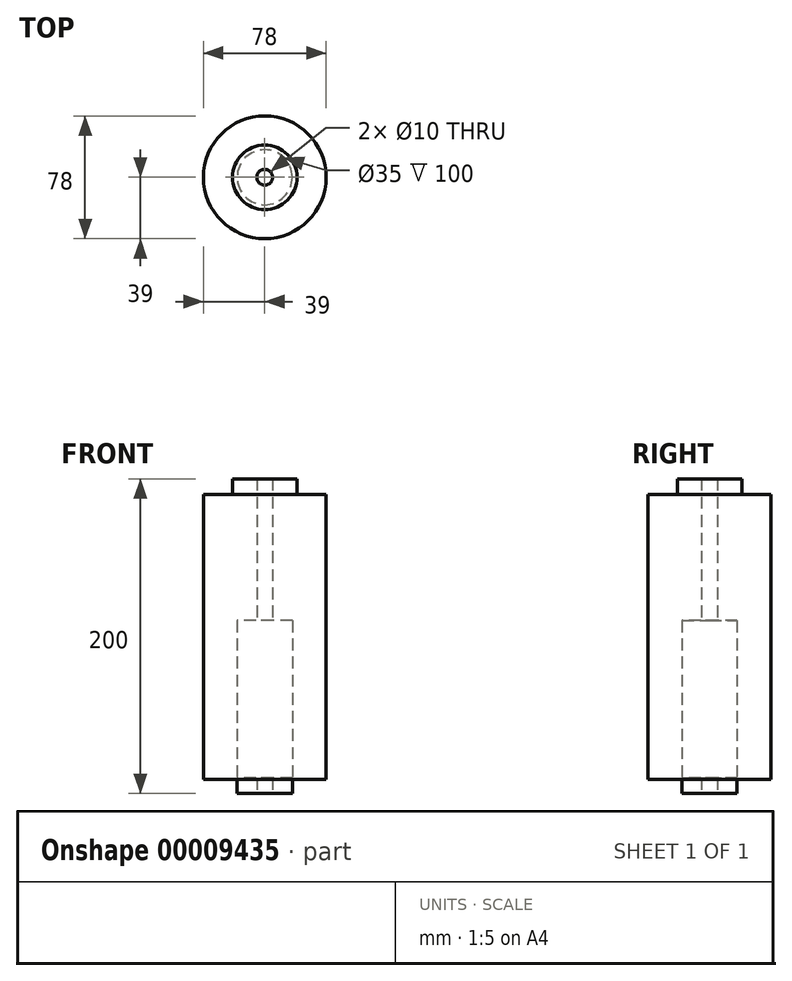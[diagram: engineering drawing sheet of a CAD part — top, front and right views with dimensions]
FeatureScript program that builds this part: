
annotation { "Feature Type Name" : "Feature", "Feature Type Description" : "" }
export const myFeature = defineFeature(function(context is Context, id is Id, definition is map)
    precondition{}
    {
        {
            var Q0;
            Q0=qCreatedBy(makeId("Top.planeOp"),FACE);
            var sketch = newSketch(context, id + "F0", { "sketchPlane" : qUnion([Q0])});
            skCircle(sketch, "E0", {"center": v(0, 0) * mm, "radius": 5 * mm});
            skCircle(sketch, "E1", {"center": v(0, 0) * mm, "radius": 17.5 * mm});
            skCircle(sketch, "E2", {"center": v(0, 0) * mm, "radius": 20.5 * mm});
            skCircle(sketch, "E3", {"center": v(0, 0) * mm, "radius": 39 * mm});
            skSolve(sketch);
        }
        {
            var Q0;
            Q0=makeQuery(id+"F0.imprint","IMPRINT",FACE,{"disambiguationData":[TD([[makeQuery(id+"F0.imprint","IMPRINT",EDGE,{"derivedFrom":sQuery(id+"F0.wireOp",EDGE,"E0")}),-1.0]])]});
            extrude(context, id + "F1", {"entities" : qUnion([Q0]), "depth" : 10 * mm});
        }
        {
            var Q0;
            Q0=makeQuery(id+"F0.imprint","IMPRINT",FACE,{"disambiguationData":[TD([[makeQuery(id+"F0.imprint","IMPRINT",EDGE,{"derivedFrom":sQuery(id+"F0.wireOp",EDGE,"E2")}),-1.0]])]});
            var Q1;
            Q1=makeQuery(id+"F0.imprint","IMPRINT",FACE,{"disambiguationData":[TD([[makeQuery(id+"F0.imprint","IMPRINT",EDGE,{"derivedFrom":sQuery(id+"F0.wireOp",EDGE,"E1")}),-1.0]])]});
            extrude(context, id + "F2", {"entities" : qUnion([Q0, Q1]), "operationType" : NewBodyOperationType.ADD, "depth" : 110 * mm, "hasSecondDirection" : true, "secondDirectionOppositeDirection" : false, "secondDirectionDepth" : 9 * mm});
        }
        {
            var Q0;
            Q0=makeQuery(id+"F2.opExtrude","CAP_FACE",FACE,{"disambiguationData":[OSD([sQuery(id+"F0.wireOp",EDGE,"E1"),sQuery(id+"F0.wireOp",EDGE,"E3")])],"isStart":false});
            extrude(context, id + "F3", {"entities" : qUnion([Q0]), "depth" : 80 * mm});
        }
        {
            var Q0;
            Q0=makeQuery(id+"F0.imprint","IMPRINT",FACE,{"disambiguationData":[TD([[makeQuery(id+"F0.imprint","IMPRINT",EDGE,{"derivedFrom":sQuery(id+"F0.wireOp",EDGE,"E1")}),-1.0]])]});
            var Q1;
            Q1=makeQuery(id+"F0.imprint","IMPRINT",FACE,{"disambiguationData":[TD([[makeQuery(id+"F0.imprint","IMPRINT",EDGE,{"derivedFrom":sQuery(id+"F0.wireOp",EDGE,"E0")}),-1.0]])]});
            extrude(context, id + "F4", {"entities" : qUnion([Q0, Q1]), "operationType" : NewBodyOperationType.ADD, "depth" : 200 * mm, "hasSecondDirection" : true, "secondDirectionOppositeDirection" : false, "secondDirectionDepth" : 110 * mm});
        }
    });
